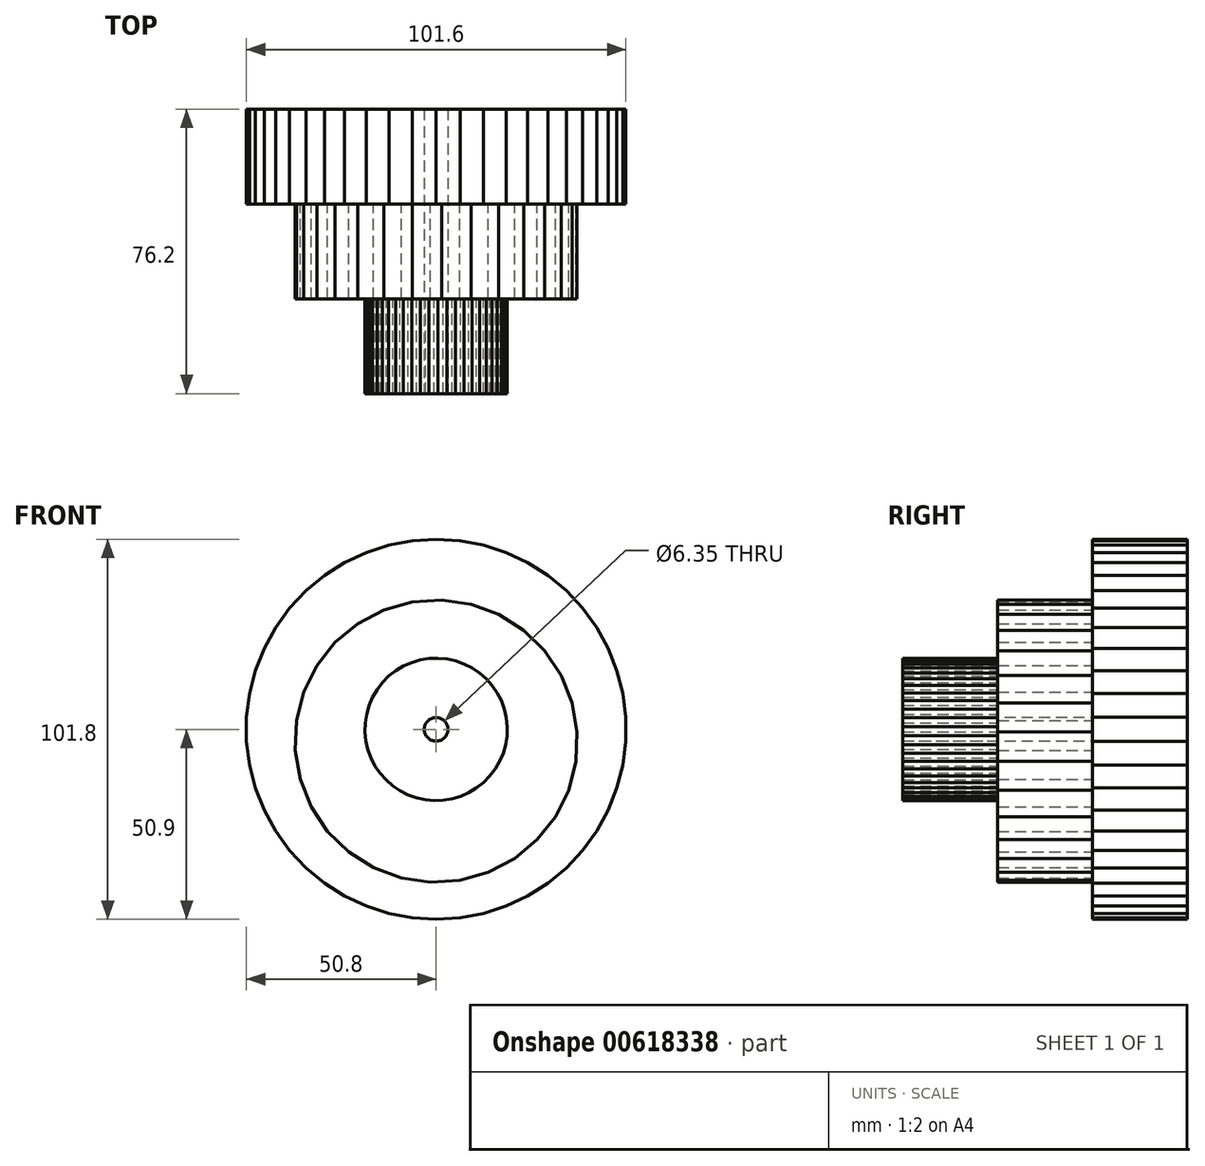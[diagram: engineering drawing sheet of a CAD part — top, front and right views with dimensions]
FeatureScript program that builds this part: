
annotation { "Feature Type Name" : "Feature", "Feature Type Description" : "" }
export const myFeature = defineFeature(function(context is Context, id is Id, definition is map)
    precondition{}
    {
        {
            var Q0;
            Q0=qCreatedBy(makeId("Front.planeOp"),FACE);
            var sketch = newSketch(context, id + "F0", { "sketchPlane" : qUnion([Q0])});
            skCircle(sketch, "E0.cCircle", {"center": v(0, 0) * mm, "radius": 50.8 * mm, "construction": true});
            skLineSegment(sketch, "E0.0", {"start": v(50.8, 3.2) * mm, "end": v(50.8, -3.2) * mm});
            skLineSegment(sketch, "E0.1", {"start": v(50.8, -3.2) * mm, "end": v(50, -9.54) * mm});
            skLineSegment(sketch, "E0.2", {"start": v(50, -9.54) * mm, "end": v(48.4, -15.73) * mm});
            skLineSegment(sketch, "E0.3", {"start": v(48.4, -15.73) * mm, "end": v(46.06, -21.67) * mm});
            skLineSegment(sketch, "E0.4", {"start": v(46.06, -21.67) * mm, "end": v(42.98, -27.27) * mm});
            skLineSegment(sketch, "E0.5", {"start": v(42.98, -27.27) * mm, "end": v(39.22, -32.45) * mm});
            skLineSegment(sketch, "E0.6", {"start": v(39.22, -32.45) * mm, "end": v(34.84, -37.1) * mm});
            skLineSegment(sketch, "E0.7", {"start": v(34.84, -37.1) * mm, "end": v(29.92, -41.18) * mm});
            skLineSegment(sketch, "E0.8", {"start": v(29.92, -41.18) * mm, "end": v(24.52, -44.6) * mm});
            skLineSegment(sketch, "E0.9", {"start": v(24.52, -44.6) * mm, "end": v(18.74, -47.33) * mm});
            skLineSegment(sketch, "E0.10", {"start": v(18.74, -47.33) * mm, "end": v(12.66, -49.3) * mm});
            skLineSegment(sketch, "E0.11", {"start": v(12.66, -49.3) * mm, "end": v(6.38, -50.5) * mm});
            skLineSegment(sketch, "E0.12", {"start": v(6.38, -50.5) * mm, "end": v(0, -50.9) * mm});
            skLineSegment(sketch, "E0.13", {"start": v(0, -50.9) * mm, "end": v(-6.38, -50.5) * mm});
            skLineSegment(sketch, "E0.14", {"start": v(-6.38, -50.5) * mm, "end": v(-12.66, -49.3) * mm});
            skLineSegment(sketch, "E0.15", {"start": v(-12.66, -49.3) * mm, "end": v(-18.74, -47.33) * mm});
            skLineSegment(sketch, "E0.16", {"start": v(-18.74, -47.33) * mm, "end": v(-24.52, -44.6) * mm});
            skLineSegment(sketch, "E0.17", {"start": v(-24.52, -44.6) * mm, "end": v(-29.92, -41.18) * mm});
            skLineSegment(sketch, "E0.18", {"start": v(-29.92, -41.18) * mm, "end": v(-34.84, -37.1) * mm});
            skLineSegment(sketch, "E0.19", {"start": v(-34.84, -37.1) * mm, "end": v(-39.22, -32.45) * mm});
            skLineSegment(sketch, "E0.20", {"start": v(-39.22, -32.45) * mm, "end": v(-42.98, -27.27) * mm});
            skLineSegment(sketch, "E0.21", {"start": v(-42.98, -27.27) * mm, "end": v(-46.06, -21.67) * mm});
            skLineSegment(sketch, "E0.22", {"start": v(-46.06, -21.67) * mm, "end": v(-48.4, -15.73) * mm});
            skLineSegment(sketch, "E0.23", {"start": v(-48.4, -15.73) * mm, "end": v(-50, -9.54) * mm});
            skLineSegment(sketch, "E0.24", {"start": v(-50, -9.54) * mm, "end": v(-50.8, -3.2) * mm});
            skLineSegment(sketch, "E0.25", {"start": v(-50.8, -3.2) * mm, "end": v(-50.8, 3.2) * mm});
            skLineSegment(sketch, "E0.26", {"start": v(-50.8, 3.2) * mm, "end": v(-50, 9.54) * mm});
            skLineSegment(sketch, "E0.27", {"start": v(-50, 9.54) * mm, "end": v(-48.4, 15.73) * mm});
            skLineSegment(sketch, "E0.28", {"start": v(-48.4, 15.73) * mm, "end": v(-46.06, 21.67) * mm});
            skLineSegment(sketch, "E0.29", {"start": v(-46.06, 21.67) * mm, "end": v(-42.98, 27.27) * mm});
            skLineSegment(sketch, "E0.30", {"start": v(-42.98, 27.27) * mm, "end": v(-39.22, 32.45) * mm});
            skLineSegment(sketch, "E0.31", {"start": v(-39.22, 32.45) * mm, "end": v(-34.84, 37.1) * mm});
            skLineSegment(sketch, "E0.32", {"start": v(-34.84, 37.1) * mm, "end": v(-29.92, 41.18) * mm});
            skLineSegment(sketch, "E0.33", {"start": v(-29.92, 41.18) * mm, "end": v(-24.52, 44.6) * mm});
            skLineSegment(sketch, "E0.34", {"start": v(-24.52, 44.6) * mm, "end": v(-18.74, 47.33) * mm});
            skLineSegment(sketch, "E0.35", {"start": v(-18.74, 47.33) * mm, "end": v(-12.66, 49.3) * mm});
            skLineSegment(sketch, "E0.36", {"start": v(-12.66, 49.3) * mm, "end": v(-6.38, 50.5) * mm});
            skLineSegment(sketch, "E0.37", {"start": v(-6.38, 50.5) * mm, "end": v(0, 50.9) * mm});
            skLineSegment(sketch, "E0.38", {"start": v(0, 50.9) * mm, "end": v(6.38, 50.5) * mm});
            skLineSegment(sketch, "E0.39", {"start": v(6.38, 50.5) * mm, "end": v(12.66, 49.3) * mm});
            skLineSegment(sketch, "E0.40", {"start": v(12.66, 49.3) * mm, "end": v(18.74, 47.33) * mm});
            skLineSegment(sketch, "E0.41", {"start": v(18.74, 47.33) * mm, "end": v(24.52, 44.6) * mm});
            skLineSegment(sketch, "E0.42", {"start": v(24.52, 44.6) * mm, "end": v(29.92, 41.18) * mm});
            skLineSegment(sketch, "E0.43", {"start": v(29.92, 41.18) * mm, "end": v(34.84, 37.1) * mm});
            skLineSegment(sketch, "E0.44", {"start": v(34.84, 37.1) * mm, "end": v(39.22, 32.45) * mm});
            skLineSegment(sketch, "E0.45", {"start": v(39.22, 32.45) * mm, "end": v(42.98, 27.27) * mm});
            skLineSegment(sketch, "E0.46", {"start": v(42.98, 27.27) * mm, "end": v(46.06, 21.67) * mm});
            skLineSegment(sketch, "E0.47", {"start": v(46.06, 21.67) * mm, "end": v(48.4, 15.73) * mm});
            skLineSegment(sketch, "E0.48", {"start": v(48.4, 15.73) * mm, "end": v(50, 9.54) * mm});
            skLineSegment(sketch, "E0.49", {"start": v(50, 9.54) * mm, "end": v(50.8, 3.2) * mm});
            skPoint(sketch, "E0.0.midPoint", {"position": v(50.8, 0) * mm});
            skSolve(sketch);
        }
        {
            var Q0;
            Q0=makeQuery(id+"F0.imprint","IMPRINT",FACE,{"disambiguationData":[TD([[makeQuery(id+"F0.imprint","IMPRINT",EDGE,{"derivedFrom":sQuery(id+"F0.wireOp",EDGE,"E0.0")}),-1.0]])]});
            extrude(context, id + "F1", {"entities" : qUnion([Q0]), "depth" : 25.4 * mm, "offsetDistance" : 25.4 * mm});
        }
        {
            var Q0;
            Q0=makeQuery(id+"F1.opExtrude","CAP_FACE",FACE,{"disambiguationData":[OSD([sQuery(id+"F0.wireOp",EDGE,"E0.0"),sQuery(id+"F0.wireOp",EDGE,"E0.1"),sQuery(id+"F0.wireOp",EDGE,"E0.2"),sQuery(id+"F0.wireOp",EDGE,"E0.3"),sQuery(id+"F0.wireOp",EDGE,"E0.4"),sQuery(id+"F0.wireOp",EDGE,"E0.5"),sQuery(id+"F0.wireOp",EDGE,"E0.6"),sQuery(id+"F0.wireOp",EDGE,"E0.7"),sQuery(id+"F0.wireOp",EDGE,"E0.8"),sQuery(id+"F0.wireOp",EDGE,"E0.9"),sQuery(id+"F0.wireOp",EDGE,"E0.10"),sQuery(id+"F0.wireOp",EDGE,"E0.11"),sQuery(id+"F0.wireOp",EDGE,"E0.12"),sQuery(id+"F0.wireOp",EDGE,"E0.13"),sQuery(id+"F0.wireOp",EDGE,"E0.14"),sQuery(id+"F0.wireOp",EDGE,"E0.15"),sQuery(id+"F0.wireOp",EDGE,"E0.16"),sQuery(id+"F0.wireOp",EDGE,"E0.17"),sQuery(id+"F0.wireOp",EDGE,"E0.18"),sQuery(id+"F0.wireOp",EDGE,"E0.19"),sQuery(id+"F0.wireOp",EDGE,"E0.20"),sQuery(id+"F0.wireOp",EDGE,"E0.21"),sQuery(id+"F0.wireOp",EDGE,"E0.22"),sQuery(id+"F0.wireOp",EDGE,"E0.23"),sQuery(id+"F0.wireOp",EDGE,"E0.24"),sQuery(id+"F0.wireOp",EDGE,"E0.25"),sQuery(id+"F0.wireOp",EDGE,"E0.26"),sQuery(id+"F0.wireOp",EDGE,"E0.27"),sQuery(id+"F0.wireOp",EDGE,"E0.28"),sQuery(id+"F0.wireOp",EDGE,"E0.29"),sQuery(id+"F0.wireOp",EDGE,"E0.30"),sQuery(id+"F0.wireOp",EDGE,"E0.31"),sQuery(id+"F0.wireOp",EDGE,"E0.32"),sQuery(id+"F0.wireOp",EDGE,"E0.33"),sQuery(id+"F0.wireOp",EDGE,"E0.34"),sQuery(id+"F0.wireOp",EDGE,"E0.35"),sQuery(id+"F0.wireOp",EDGE,"E0.36"),sQuery(id+"F0.wireOp",EDGE,"E0.37"),sQuery(id+"F0.wireOp",EDGE,"E0.38"),sQuery(id+"F0.wireOp",EDGE,"E0.39"),sQuery(id+"F0.wireOp",EDGE,"E0.40"),sQuery(id+"F0.wireOp",EDGE,"E0.41"),sQuery(id+"F0.wireOp",EDGE,"E0.42"),sQuery(id+"F0.wireOp",EDGE,"E0.43"),sQuery(id+"F0.wireOp",EDGE,"E0.44"),sQuery(id+"F0.wireOp",EDGE,"E0.45"),sQuery(id+"F0.wireOp",EDGE,"E0.46"),sQuery(id+"F0.wireOp",EDGE,"E0.47"),sQuery(id+"F0.wireOp",EDGE,"E0.48"),sQuery(id+"F0.wireOp",EDGE,"E0.49")])],"isStart":false});
            var sketch = newSketch(context, id + "F2", { "sketchPlane" : qUnion([Q0])});
            skCircle(sketch, "E1.cCircle", {"center": v(0, -3.15) * mm, "radius": 37.62 * mm, "construction": true});
            skLineSegment(sketch, "E1.0", {"start": v(35.47, -16.27) * mm, "end": v(31.97, -23.36) * mm});
            skLineSegment(sketch, "E1.1", {"start": v(31.97, -23.36) * mm, "end": v(27.07, -29.56) * mm});
            skLineSegment(sketch, "E1.2", {"start": v(27.07, -29.56) * mm, "end": v(20.99, -34.61) * mm});
            skLineSegment(sketch, "E1.3", {"start": v(20.99, -34.61) * mm, "end": v(13.99, -38.29) * mm});
            skLineSegment(sketch, "E1.4", {"start": v(13.99, -38.29) * mm, "end": v(6.37, -40.43) * mm});
            skLineSegment(sketch, "E1.5", {"start": v(6.37, -40.43) * mm, "end": v(-1.52, -40.94) * mm});
            skLineSegment(sketch, "E1.6", {"start": v(-1.52, -40.94) * mm, "end": v(-9.34, -39.8) * mm});
            skLineSegment(sketch, "E1.7", {"start": v(-9.34, -39.8) * mm, "end": v(-16.76, -37.06) * mm});
            skLineSegment(sketch, "E1.8", {"start": v(-16.76, -37.06) * mm, "end": v(-23.44, -32.83) * mm});
            skLineSegment(sketch, "E1.9", {"start": v(-23.44, -32.83) * mm, "end": v(-29.1, -27.3) * mm});
            skLineSegment(sketch, "E1.10", {"start": v(-29.1, -27.3) * mm, "end": v(-33.49, -20.73) * mm});
            skLineSegment(sketch, "E1.11", {"start": v(-33.49, -20.73) * mm, "end": v(-36.41, -13.38) * mm});
            skLineSegment(sketch, "E1.12", {"start": v(-36.41, -13.38) * mm, "end": v(-37.74, -5.59) * mm});
            skLineSegment(sketch, "E1.13", {"start": v(-37.74, -5.59) * mm, "end": v(-37.43, 2.31) * mm});
            skLineSegment(sketch, "E1.14", {"start": v(-37.43, 2.31) * mm, "end": v(-35.47, 9.98) * mm});
            skLineSegment(sketch, "E1.15", {"start": v(-35.47, 9.98) * mm, "end": v(-31.97, 17.06) * mm});
            skLineSegment(sketch, "E1.16", {"start": v(-31.97, 17.06) * mm, "end": v(-27.07, 23.27) * mm});
            skLineSegment(sketch, "E1.17", {"start": v(-27.07, 23.27) * mm, "end": v(-20.99, 28.32) * mm});
            skLineSegment(sketch, "E1.18", {"start": v(-20.99, 28.32) * mm, "end": v(-13.99, 32) * mm});
            skLineSegment(sketch, "E1.19", {"start": v(-13.99, 32) * mm, "end": v(-6.37, 34.14) * mm});
            skLineSegment(sketch, "E1.20", {"start": v(-6.37, 34.14) * mm, "end": v(1.52, 34.65) * mm});
            skLineSegment(sketch, "E1.21", {"start": v(1.52, 34.65) * mm, "end": v(9.34, 33.5) * mm});
            skLineSegment(sketch, "E1.22", {"start": v(9.34, 33.5) * mm, "end": v(16.76, 30.76) * mm});
            skLineSegment(sketch, "E1.23", {"start": v(16.76, 30.76) * mm, "end": v(23.44, 26.54) * mm});
            skLineSegment(sketch, "E1.24", {"start": v(23.44, 26.54) * mm, "end": v(29.1, 21.01) * mm});
            skLineSegment(sketch, "E1.25", {"start": v(29.1, 21.01) * mm, "end": v(33.49, 14.44) * mm});
            skLineSegment(sketch, "E1.26", {"start": v(33.49, 14.44) * mm, "end": v(36.41, 7.09) * mm});
            skLineSegment(sketch, "E1.27", {"start": v(36.41, 7.09) * mm, "end": v(37.74, -0.7) * mm});
            skLineSegment(sketch, "E1.28", {"start": v(37.74, -0.7) * mm, "end": v(37.43, -8.6) * mm});
            skLineSegment(sketch, "E1.29", {"start": v(37.43, -8.6) * mm, "end": v(35.47, -16.27) * mm});
            skPoint(sketch, "E1.0.midPoint", {"position": v(33.72, -19.81) * mm});
            skSolve(sketch);
        }
        {
            var Q0;
            Q0=makeQuery(id+"F2.imprint","IMPRINT",FACE,{"disambiguationData":[TD([[makeQuery(id+"F2.imprint","IMPRINT",EDGE,{"derivedFrom":sQuery(id+"F2.wireOp",EDGE,"E1.0")}),-1.0]])]});
            extrude(context, id + "F3", {"entities" : qUnion([Q0]), "operationType" : NewBodyOperationType.ADD, "depth" : 25.4 * mm, "offsetDistance" : 25.4 * mm});
        }
        {
            var Q0;
            Q0=makeQuery(id+"F3.opExtrude","CAP_FACE",FACE,{"disambiguationData":[OSD([sQuery(id+"F2.wireOp",EDGE,"E1.0"),sQuery(id+"F2.wireOp",EDGE,"E1.1"),sQuery(id+"F2.wireOp",EDGE,"E1.2"),sQuery(id+"F2.wireOp",EDGE,"E1.3"),sQuery(id+"F2.wireOp",EDGE,"E1.4"),sQuery(id+"F2.wireOp",EDGE,"E1.5"),sQuery(id+"F2.wireOp",EDGE,"E1.6"),sQuery(id+"F2.wireOp",EDGE,"E1.7"),sQuery(id+"F2.wireOp",EDGE,"E1.8"),sQuery(id+"F2.wireOp",EDGE,"E1.9"),sQuery(id+"F2.wireOp",EDGE,"E1.10"),sQuery(id+"F2.wireOp",EDGE,"E1.11"),sQuery(id+"F2.wireOp",EDGE,"E1.12"),sQuery(id+"F2.wireOp",EDGE,"E1.13"),sQuery(id+"F2.wireOp",EDGE,"E1.14"),sQuery(id+"F2.wireOp",EDGE,"E1.15"),sQuery(id+"F2.wireOp",EDGE,"E1.16"),sQuery(id+"F2.wireOp",EDGE,"E1.17"),sQuery(id+"F2.wireOp",EDGE,"E1.18"),sQuery(id+"F2.wireOp",EDGE,"E1.19"),sQuery(id+"F2.wireOp",EDGE,"E1.20"),sQuery(id+"F2.wireOp",EDGE,"E1.21"),sQuery(id+"F2.wireOp",EDGE,"E1.22"),sQuery(id+"F2.wireOp",EDGE,"E1.23"),sQuery(id+"F2.wireOp",EDGE,"E1.24"),sQuery(id+"F2.wireOp",EDGE,"E1.25"),sQuery(id+"F2.wireOp",EDGE,"E1.26"),sQuery(id+"F2.wireOp",EDGE,"E1.27"),sQuery(id+"F2.wireOp",EDGE,"E1.28"),sQuery(id+"F2.wireOp",EDGE,"E1.29")])],"isStart":false});
            var sketch = newSketch(context, id + "F4", { "sketchPlane" : qUnion([Q0])});
            skCircle(sketch, "E2.cCircle", {"center": v(0, 0) * mm, "radius": 19.03 * mm, "construction": true});
            skLineSegment(sketch, "E2.0", {"start": v(17.03, -8.57) * mm, "end": v(15.82, -10.64) * mm});
            skLineSegment(sketch, "E2.1", {"start": v(15.82, -10.64) * mm, "end": v(14.36, -12.54) * mm});
            skLineSegment(sketch, "E2.2", {"start": v(14.36, -12.54) * mm, "end": v(12.68, -14.24) * mm});
            skLineSegment(sketch, "E2.3", {"start": v(12.68, -14.24) * mm, "end": v(10.8, -15.72) * mm});
            skLineSegment(sketch, "E2.4", {"start": v(10.8, -15.72) * mm, "end": v(8.74, -16.94) * mm});
            skLineSegment(sketch, "E2.5", {"start": v(8.74, -16.94) * mm, "end": v(6.55, -17.9) * mm});
            skLineSegment(sketch, "E2.6", {"start": v(6.55, -17.9) * mm, "end": v(4.25, -18.58) * mm});
            skLineSegment(sketch, "E2.7", {"start": v(4.25, -18.58) * mm, "end": v(1.89, -18.97) * mm});
            skLineSegment(sketch, "E2.8", {"start": v(1.89, -18.97) * mm, "end": v(-0.5, -19.06) * mm});
            skLineSegment(sketch, "E2.9", {"start": v(-0.5, -19.06) * mm, "end": v(-2.89, -18.84) * mm});
            skLineSegment(sketch, "E2.10", {"start": v(-2.89, -18.84) * mm, "end": v(-5.23, -18.33) * mm});
            skLineSegment(sketch, "E2.11", {"start": v(-5.23, -18.33) * mm, "end": v(-7.49, -17.53) * mm});
            skLineSegment(sketch, "E2.12", {"start": v(-7.49, -17.53) * mm, "end": v(-9.62, -16.46) * mm});
            skLineSegment(sketch, "E2.13", {"start": v(-9.62, -16.46) * mm, "end": v(-11.61, -15.12) * mm});
            skLineSegment(sketch, "E2.14", {"start": v(-11.61, -15.12) * mm, "end": v(-13.41, -13.55) * mm});
            skLineSegment(sketch, "E2.15", {"start": v(-13.41, -13.55) * mm, "end": v(-15, -11.76) * mm});
            skLineSegment(sketch, "E2.16", {"start": v(-15, -11.76) * mm, "end": v(-16.36, -9.79) * mm});
            skLineSegment(sketch, "E2.17", {"start": v(-16.36, -9.79) * mm, "end": v(-17.46, -7.66) * mm});
            skLineSegment(sketch, "E2.18", {"start": v(-17.46, -7.66) * mm, "end": v(-18.28, -5.4) * mm});
            skLineSegment(sketch, "E2.19", {"start": v(-18.28, -5.4) * mm, "end": v(-18.82, -3.07) * mm});
            skLineSegment(sketch, "E2.20", {"start": v(-18.82, -3.07) * mm, "end": v(-19.05, -0.7) * mm});
            skLineSegment(sketch, "E2.21", {"start": v(-19.05, -0.7) * mm, "end": v(-18.99, 1.7) * mm});
            skLineSegment(sketch, "E2.22", {"start": v(-18.99, 1.7) * mm, "end": v(-18.63, 4.07) * mm});
            skLineSegment(sketch, "E2.23", {"start": v(-18.63, 4.07) * mm, "end": v(-17.97, 6.37) * mm});
            skLineSegment(sketch, "E2.24", {"start": v(-17.97, 6.37) * mm, "end": v(-17.03, 8.57) * mm});
            skLineSegment(sketch, "E2.25", {"start": v(-17.03, 8.57) * mm, "end": v(-15.82, 10.64) * mm});
            skLineSegment(sketch, "E2.26", {"start": v(-15.82, 10.64) * mm, "end": v(-14.36, 12.54) * mm});
            skLineSegment(sketch, "E2.27", {"start": v(-14.36, 12.54) * mm, "end": v(-12.68, 14.24) * mm});
            skLineSegment(sketch, "E2.28", {"start": v(-12.68, 14.24) * mm, "end": v(-10.8, 15.72) * mm});
            skLineSegment(sketch, "E2.29", {"start": v(-10.8, 15.72) * mm, "end": v(-8.74, 16.94) * mm});
            skLineSegment(sketch, "E2.30", {"start": v(-8.74, 16.94) * mm, "end": v(-6.55, 17.9) * mm});
            skLineSegment(sketch, "E2.31", {"start": v(-6.55, 17.9) * mm, "end": v(-4.25, 18.58) * mm});
            skLineSegment(sketch, "E2.32", {"start": v(-4.25, 18.58) * mm, "end": v(-1.89, 18.97) * mm});
            skLineSegment(sketch, "E2.33", {"start": v(-1.89, 18.97) * mm, "end": v(0.5, 19.06) * mm});
            skLineSegment(sketch, "E2.34", {"start": v(0.5, 19.06) * mm, "end": v(2.89, 18.84) * mm});
            skLineSegment(sketch, "E2.35", {"start": v(2.89, 18.84) * mm, "end": v(5.23, 18.33) * mm});
            skLineSegment(sketch, "E2.36", {"start": v(5.23, 18.33) * mm, "end": v(7.49, 17.53) * mm});
            skLineSegment(sketch, "E2.37", {"start": v(7.49, 17.53) * mm, "end": v(9.62, 16.46) * mm});
            skLineSegment(sketch, "E2.38", {"start": v(9.62, 16.46) * mm, "end": v(11.61, 15.12) * mm});
            skLineSegment(sketch, "E2.39", {"start": v(11.61, 15.12) * mm, "end": v(13.41, 13.55) * mm});
            skLineSegment(sketch, "E2.40", {"start": v(13.41, 13.55) * mm, "end": v(15, 11.76) * mm});
            skLineSegment(sketch, "E2.41", {"start": v(15, 11.76) * mm, "end": v(16.36, 9.79) * mm});
            skLineSegment(sketch, "E2.42", {"start": v(16.36, 9.79) * mm, "end": v(17.46, 7.66) * mm});
            skLineSegment(sketch, "E2.43", {"start": v(17.46, 7.66) * mm, "end": v(18.28, 5.4) * mm});
            skLineSegment(sketch, "E2.44", {"start": v(18.28, 5.4) * mm, "end": v(18.82, 3.07) * mm});
            skLineSegment(sketch, "E2.45", {"start": v(18.82, 3.07) * mm, "end": v(19.05, 0.7) * mm});
            skLineSegment(sketch, "E2.46", {"start": v(19.05, 0.7) * mm, "end": v(18.99, -1.7) * mm});
            skLineSegment(sketch, "E2.47", {"start": v(18.99, -1.7) * mm, "end": v(18.63, -4.07) * mm});
            skLineSegment(sketch, "E2.48", {"start": v(18.63, -4.07) * mm, "end": v(17.97, -6.37) * mm});
            skLineSegment(sketch, "E2.49", {"start": v(17.97, -6.37) * mm, "end": v(17.03, -8.57) * mm});
            skPoint(sketch, "E2.0.midPoint", {"position": v(16.42, -9.6) * mm});
            skSolve(sketch);
        }
        {
            var Q0;
            Q0=makeQuery(id+"F4.imprint","IMPRINT",FACE,{"disambiguationData":[TD([[makeQuery(id+"F4.imprint","IMPRINT",EDGE,{"derivedFrom":sQuery(id+"F4.wireOp",EDGE,"E2.0")}),-1.0]])]});
            extrude(context, id + "F5", {"entities" : qUnion([Q0]), "operationType" : NewBodyOperationType.ADD, "depth" : 25.4 * mm, "offsetDistance" : 25.4 * mm});
        }
        {
            var Q0;
            Q0=makeQuery(id+"F5.opExtrude","CAP_FACE",FACE,{"disambiguationData":[OSD([sQuery(id+"F4.wireOp",EDGE,"E2.0"),sQuery(id+"F4.wireOp",EDGE,"E2.1"),sQuery(id+"F4.wireOp",EDGE,"E2.2"),sQuery(id+"F4.wireOp",EDGE,"E2.3"),sQuery(id+"F4.wireOp",EDGE,"E2.4"),sQuery(id+"F4.wireOp",EDGE,"E2.5"),sQuery(id+"F4.wireOp",EDGE,"E2.6"),sQuery(id+"F4.wireOp",EDGE,"E2.7"),sQuery(id+"F4.wireOp",EDGE,"E2.8"),sQuery(id+"F4.wireOp",EDGE,"E2.9"),sQuery(id+"F4.wireOp",EDGE,"E2.10"),sQuery(id+"F4.wireOp",EDGE,"E2.11"),sQuery(id+"F4.wireOp",EDGE,"E2.12"),sQuery(id+"F4.wireOp",EDGE,"E2.13"),sQuery(id+"F4.wireOp",EDGE,"E2.14"),sQuery(id+"F4.wireOp",EDGE,"E2.15"),sQuery(id+"F4.wireOp",EDGE,"E2.16"),sQuery(id+"F4.wireOp",EDGE,"E2.17"),sQuery(id+"F4.wireOp",EDGE,"E2.18"),sQuery(id+"F4.wireOp",EDGE,"E2.19"),sQuery(id+"F4.wireOp",EDGE,"E2.20"),sQuery(id+"F4.wireOp",EDGE,"E2.21"),sQuery(id+"F4.wireOp",EDGE,"E2.22"),sQuery(id+"F4.wireOp",EDGE,"E2.23"),sQuery(id+"F4.wireOp",EDGE,"E2.24"),sQuery(id+"F4.wireOp",EDGE,"E2.25"),sQuery(id+"F4.wireOp",EDGE,"E2.26"),sQuery(id+"F4.wireOp",EDGE,"E2.27"),sQuery(id+"F4.wireOp",EDGE,"E2.28"),sQuery(id+"F4.wireOp",EDGE,"E2.29"),sQuery(id+"F4.wireOp",EDGE,"E2.30"),sQuery(id+"F4.wireOp",EDGE,"E2.31"),sQuery(id+"F4.wireOp",EDGE,"E2.32"),sQuery(id+"F4.wireOp",EDGE,"E2.33"),sQuery(id+"F4.wireOp",EDGE,"E2.34"),sQuery(id+"F4.wireOp",EDGE,"E2.35"),sQuery(id+"F4.wireOp",EDGE,"E2.36"),sQuery(id+"F4.wireOp",EDGE,"E2.37"),sQuery(id+"F4.wireOp",EDGE,"E2.38"),sQuery(id+"F4.wireOp",EDGE,"E2.39"),sQuery(id+"F4.wireOp",EDGE,"E2.40"),sQuery(id+"F4.wireOp",EDGE,"E2.41"),sQuery(id+"F4.wireOp",EDGE,"E2.42"),sQuery(id+"F4.wireOp",EDGE,"E2.43"),sQuery(id+"F4.wireOp",EDGE,"E2.44"),sQuery(id+"F4.wireOp",EDGE,"E2.45"),sQuery(id+"F4.wireOp",EDGE,"E2.46"),sQuery(id+"F4.wireOp",EDGE,"E2.47"),sQuery(id+"F4.wireOp",EDGE,"E2.48"),sQuery(id+"F4.wireOp",EDGE,"E2.49")])],"isStart":false});
            var sketch = newSketch(context, id + "F6", { "sketchPlane" : qUnion([Q0])});
            skCircle(sketch, "E3", {"center": v(0, 0) * mm, "radius": 2.4 * mm});
            skSolve(sketch);
        }
        {
            var Q0;
            Q0=sQuery(id+"F6.wireOp",VERTEX,"E3.center");
            var Q1;
            Q1=makeQuery(id+"F1.opExtrude","SWEPT_BODY",BODY,{"disambiguationData":[OSD([sQuery(id+"F0.wireOp",EDGE,"E0.0"),sQuery(id+"F0.wireOp",EDGE,"E0.1"),sQuery(id+"F0.wireOp",EDGE,"E0.2"),sQuery(id+"F0.wireOp",EDGE,"E0.3"),sQuery(id+"F0.wireOp",EDGE,"E0.4"),sQuery(id+"F0.wireOp",EDGE,"E0.5"),sQuery(id+"F0.wireOp",EDGE,"E0.6"),sQuery(id+"F0.wireOp",EDGE,"E0.7"),sQuery(id+"F0.wireOp",EDGE,"E0.8"),sQuery(id+"F0.wireOp",EDGE,"E0.9"),sQuery(id+"F0.wireOp",EDGE,"E0.10"),sQuery(id+"F0.wireOp",EDGE,"E0.11"),sQuery(id+"F0.wireOp",EDGE,"E0.12"),sQuery(id+"F0.wireOp",EDGE,"E0.13"),sQuery(id+"F0.wireOp",EDGE,"E0.14"),sQuery(id+"F0.wireOp",EDGE,"E0.15"),sQuery(id+"F0.wireOp",EDGE,"E0.16"),sQuery(id+"F0.wireOp",EDGE,"E0.17"),sQuery(id+"F0.wireOp",EDGE,"E0.18"),sQuery(id+"F0.wireOp",EDGE,"E0.19"),sQuery(id+"F0.wireOp",EDGE,"E0.20"),sQuery(id+"F0.wireOp",EDGE,"E0.21"),sQuery(id+"F0.wireOp",EDGE,"E0.22"),sQuery(id+"F0.wireOp",EDGE,"E0.23"),sQuery(id+"F0.wireOp",EDGE,"E0.24"),sQuery(id+"F0.wireOp",EDGE,"E0.25"),sQuery(id+"F0.wireOp",EDGE,"E0.26"),sQuery(id+"F0.wireOp",EDGE,"E0.27"),sQuery(id+"F0.wireOp",EDGE,"E0.28"),sQuery(id+"F0.wireOp",EDGE,"E0.29"),sQuery(id+"F0.wireOp",EDGE,"E0.30"),sQuery(id+"F0.wireOp",EDGE,"E0.31"),sQuery(id+"F0.wireOp",EDGE,"E0.32"),sQuery(id+"F0.wireOp",EDGE,"E0.33"),sQuery(id+"F0.wireOp",EDGE,"E0.34"),sQuery(id+"F0.wireOp",EDGE,"E0.35"),sQuery(id+"F0.wireOp",EDGE,"E0.36"),sQuery(id+"F0.wireOp",EDGE,"E0.37"),sQuery(id+"F0.wireOp",EDGE,"E0.38"),sQuery(id+"F0.wireOp",EDGE,"E0.39"),sQuery(id+"F0.wireOp",EDGE,"E0.40"),sQuery(id+"F0.wireOp",EDGE,"E0.41"),sQuery(id+"F0.wireOp",EDGE,"E0.42"),sQuery(id+"F0.wireOp",EDGE,"E0.43"),sQuery(id+"F0.wireOp",EDGE,"E0.44"),sQuery(id+"F0.wireOp",EDGE,"E0.45"),sQuery(id+"F0.wireOp",EDGE,"E0.46"),sQuery(id+"F0.wireOp",EDGE,"E0.47"),sQuery(id+"F0.wireOp",EDGE,"E0.48"),sQuery(id+"F0.wireOp",EDGE,"E0.49")])]});
            hole(context, id + "F7", {"style" : HoleStyle.SIMPLE, "endStyle" : HoleEndStyle.THROUGH, "holeDiameter" : 6.35 * mm, "majorDiameter" : 6.35 * mm, "isTappedThrough" : true, "tappedDepth" : 12.7 * mm, "tapClearance" : 3, "locations" : qUnion([Q0]), "scope" : qUnion([Q1])});
        }
    });
